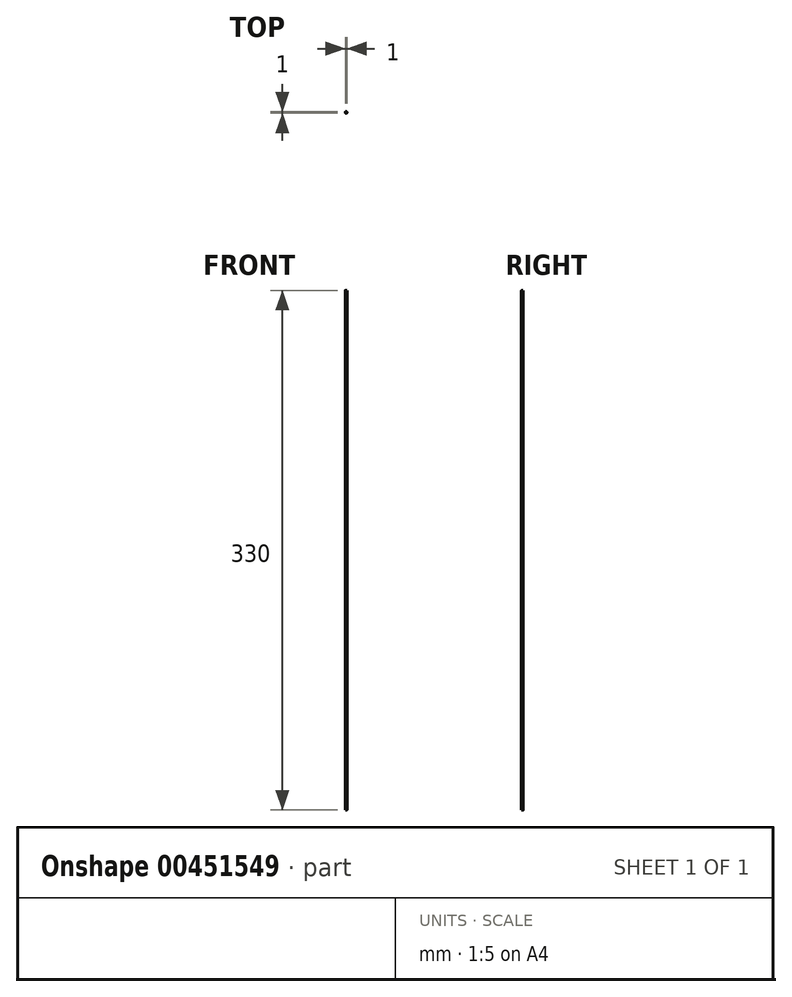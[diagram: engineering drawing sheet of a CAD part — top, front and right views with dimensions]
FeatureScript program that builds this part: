
annotation { "Feature Type Name" : "Feature", "Feature Type Description" : "" }
export const myFeature = defineFeature(function(context is Context, id is Id, definition is map)
    precondition{}
    {
        {
            var Q0;
            Q0=qCreatedBy(makeId("Top.planeOp"),FACE);
            var sketch = newSketch(context, id + "F0", { "sketchPlane" : qUnion([Q0])});
            skCircle(sketch, "E0", {"center": v(0, 0) * mm, "radius": 0.5 * mm});
            skSolve(sketch);
        }
        {
            var Q0;
            Q0=makeQuery(id+"F0.imprint","IMPRINT",FACE,{"disambiguationData":[TD([[makeQuery(id+"F0.imprint","IMPRINT",EDGE,{"derivedFrom":sQuery(id+"F0.wireOp",EDGE,"E0")}),1.0]])]});
            extrude(context, id + "F1", {"entities" : qUnion([Q0]), "depth" : 330 * mm, "offsetDistance" : 25 * mm});
        }
    });
